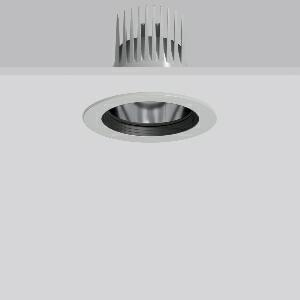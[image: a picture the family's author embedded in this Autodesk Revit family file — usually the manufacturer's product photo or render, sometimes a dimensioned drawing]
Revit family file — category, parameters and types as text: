
# Revit family: heledon_maxi_e_901772_004_d20a
name_source: partatom
category: Lighting Fixtures
units: mm (PartAtom-declared; Revit-internal decimal feet)

## family parameters
Cut with Voids When Loaded = No
Host = Face
Light Source = No
Part Type = Normal
Room Calculation Point = No
Round Connector Dimension = Use Diameter
Shared = No

## types (1)
- HELEDON maxi E (1 x LED Modul 932 fresh meat, 2150 lm, 3200)
    Apparent Load = 33 VA
    Approval mark = CE
    CIE Flux Codes = 100 100 100 100 100
    Color Rendering = 90
    Color Temperature = 3200
    Default Elevation = 1800 mm
    Description = Series: HELEDON maxi
Round recessed downlight. Housing: die-cast aluminium, powder-coated. Black plastic ring and recessed LED to prevent glare from the side. Optical assembly with reflector made of MIRO-Silver with 98% total light reflection for outstanding efficiency - can be changed without tools. Special LED for illumination of meat included. Suitable for Recessed ceiling mounting. Installation without tools thanks to spring fastening system. Including separate LED converter with connecting cable 600 mm.High quality converter without flickering and stroboscopic effect. Through-wiring box (5 pole) available as accessory. The following accessories can be mounted without use of tools: interchangeable lenses, decorative glasses, honeycomb louvre, clear and frosted diffusers, white interchangeable plastic ring. 
Colour: silver
Diameter: 162 mm
Height: 3 mm
Cut-out diameter: 152 mm
Recess height: 200 mm
Luminaire: recess height: 135 mm
Lamp: LED
Socket: without socket
Colour temperature: fresh meat
System power: 33 W
Rated luminous flux: 2150 lm
Luminous efficiency: 65 lm/W
Control gear: Regulated power supply
Protection class: II
Type of protection: IP 20
    Height = 0 mm  [stored 0 ft]
    Lamp = 1 x LED Modul 932 fresh meat
    Lamp Light Flux = 2150 lm
    Lamp count = 1
    Length = 162 mm
    Lifetime = 50000 h
    Luminous efficacy = 65 lm/W
    Manufacturer = RZB
    ModVariant = No
    Model = 901772.004
    Mounting Place = Ceiling
    Mounting Type = Recessed
    Number of Poles = 1
    OnlyDefault = Yes
    Power Factor = 1
    Product Name = HELEDON maxi E
    Product group = Recessed downlights
    ProductGroupID = 402
    Protection Class = Protection class II
    Protection Degree = IP 20
    RLX_Detail_Level = 1
    RLX_Emergency_Light_Flux = 0 lm
    RLX_Emergency_Type = 0
    RLX_Emergency_Type_DB = No
    RlxData = <blob elided: 119269 chars, md5=1da024bb>
    Socket = socket
    Standby Power = 0 W
    System Light Flux = 2150 lm
    System Power = 33 W
    Type Comments = Product without accessories
    Type Image = 901662.004.jpg
    URL = http://relux.com
    VarID = ---
    Voltage = 230 V
    Voltage Range = 220-240 V
    Weight = 0.00 kg
    Width = 0 mm  [stored 0 ft]

note: [stored X ft] marks values corroborated as IEEE doubles in the binary element streams (Revit-internal decimal feet)

## geometry (parser evidence)
native form markers: Blend x4, Sweep x11
no freeform markers — native parametric forms only
